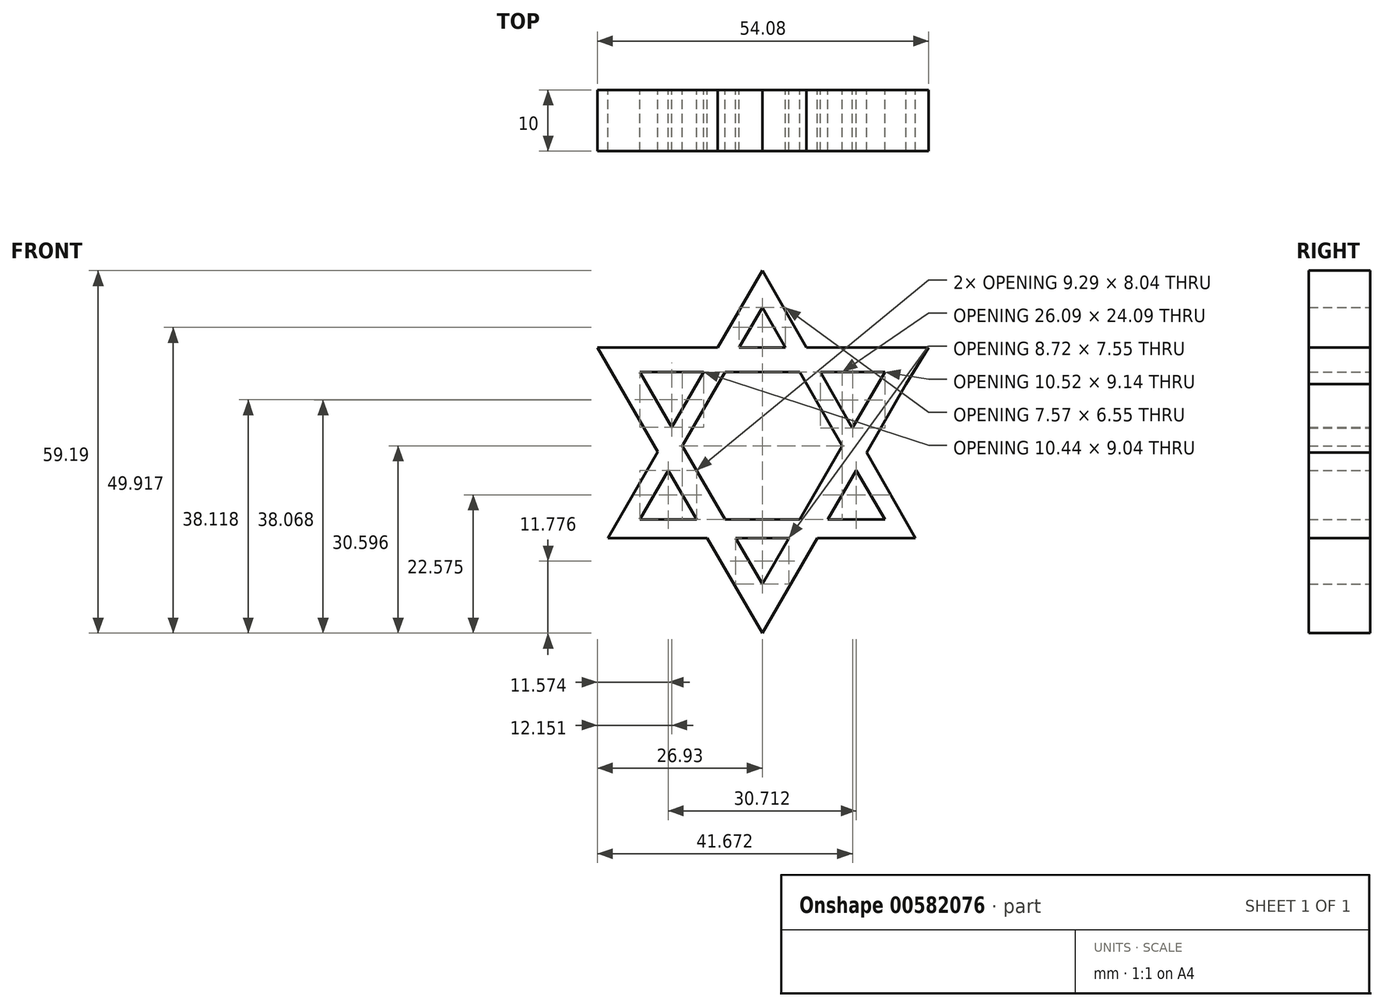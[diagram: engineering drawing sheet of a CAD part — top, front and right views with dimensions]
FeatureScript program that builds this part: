
annotation { "Feature Type Name" : "Feature", "Feature Type Description" : "" }
export const myFeature = defineFeature(function(context is Context, id is Id, definition is map)
    precondition{}
    {
        {
            var Q0;
            Q0=qCreatedBy(makeId("Front.planeOp"),FACE);
            var sketch = newSketch(context, id + "F0", { "sketchPlane" : qUnion([Q0])});
            skLineSegment(sketch, "E0", {"start": v(0, -49.6) * mm, "end": v(0, 49.74) * mm, "construction": true});
            skLineSegment(sketch, "E1", {"start": v(-9.56, 0) * mm, "end": v(56.5, 0) * mm, "construction": true});
            skLineSegment(sketch, "E2", {"start": v(0, -34.64) * mm, "end": v(-20, 0) * mm});
            skLineSegment(sketch, "E3", {"start": v(-20, 0) * mm, "end": v(20, 0) * mm});
            skLineSegment(sketch, "E4", {"start": v(20, 0) * mm, "end": v(0, -34.64) * mm});
            skLineSegment(sketch, "E5", {"start": v(-20, -24.09) * mm, "end": v(0, 10.55) * mm});
            skLineSegment(sketch, "E6", {"start": v(0, 10.55) * mm, "end": v(20, -24.09) * mm});
            skLineSegment(sketch, "E7", {"start": v(-20, -24.09) * mm, "end": v(20, -24.09) * mm});
            skLineSegment(sketch, "E8", {"start": v(25, -27.09) * mm, "end": v(-25.2, -27.09) * mm});
            skLineSegment(sketch, "E9", {"start": v(-25.2, -27.09) * mm, "end": v(0, 16.55) * mm});
            skLineSegment(sketch, "E10", {"start": v(0, 16.55) * mm, "end": v(25, -27.09) * mm});
            skLineSegment(sketch, "E11.0", {"start": v(0, -42.64) * mm, "end": v(-23.46, -2) * mm});
            skLineSegment(sketch, "E11.1", {"start": v(23.46, -2) * mm, "end": v(0, -42.64) * mm});
            skPoint(sketch, "E12.orphan", {"position": v(-51.85, 0) * mm});
            skLineSegment(sketch, "E13.0", {"start": v(-20, 4) * mm, "end": v(20, 4) * mm});
            skLineSegment(sketch, "E14", {"start": v(-23.46, -2) * mm, "end": v(-26.93, 4) * mm});
            skLineSegment(sketch, "E15", {"start": v(-26.93, 4) * mm, "end": v(-20, 4) * mm});
            skLineSegment(sketch, "E16", {"start": v(20, 4) * mm, "end": v(27.15, 4) * mm});
            skPoint(sketch, "E16.endSnap0", {"position": v(0, 4) * mm});
            skLineSegment(sketch, "E17", {"start": v(27.15, 4) * mm, "end": v(23.46, -2) * mm});
            skSolve(sketch);
        }
        {
            var Q0;
            {var subQ0=sQuery(id+"F0.wireOp",EDGE,"E7");var subQ1=sQuery(id+"F0.wireOp",EDGE,"E2");var subQ2=makeQuery(id+"F0.imprint","INTERSECT",VERTEX,{"derivedFrom":[subQ1,subQ0]});Q0=makeQuery(id+"F0.imprint","IMPRINT",FACE,{"disambiguationData":[TD([[makeQuery(id+"F0.imprint","IMPRINT",EDGE,{"disambiguationData":[TD([[subQ2,-1.0]])],"derivedFrom":subQ1}),1.0]])]});}
            var Q1;
            {var subQ3=sQuery(id+"F0.wireOp",EDGE,"E2");var subQ5=sQuery(id+"F0.wireOp",EDGE,"E4");var subQ6=makeQuery(id+"F0.imprint","INTERSECT",VERTEX,{"derivedFrom":[subQ3,subQ5]});Q1=makeQuery(id+"F0.imprint","IMPRINT",FACE,{"disambiguationData":[TD([[makeQuery(id+"F0.imprint","IMPRINT",EDGE,{"disambiguationData":[TD([[subQ6,-1.0]])],"derivedFrom":subQ3}),1.0]])]});}
            var Q2;
            {var subQ0=sQuery(id+"F0.wireOp",EDGE,"E6");var subQ1=sQuery(id+"F0.wireOp",EDGE,"E4");var subQ2=makeQuery(id+"F0.imprint","INTERSECT",VERTEX,{"derivedFrom":[subQ1,subQ0]});Q2=makeQuery(id+"F0.imprint","IMPRINT",FACE,{"disambiguationData":[TD([[makeQuery(id+"F0.imprint","IMPRINT",EDGE,{"disambiguationData":[TD([[subQ2,-1.0]])],"derivedFrom":subQ1}),1.0]])]});}
            var Q3;
            {var subQ11=sQuery(id+"F0.wireOp",EDGE,"E16");Q3=makeQuery(id+"F0.imprint","IMPRINT",FACE,{"disambiguationData":[TD([[makeQuery(id+"F0.imprint","IMPRINT",EDGE,{"derivedFrom":subQ11}),-1.0]])]});}
            var Q4;
            {var subQ0=sQuery(id+"F0.wireOp",EDGE,"E5");var subQ1=sQuery(id+"F0.wireOp",EDGE,"E3");var subQ2=makeQuery(id+"F0.imprint","INTERSECT",VERTEX,{"derivedFrom":[subQ1,subQ0]});Q4=makeQuery(id+"F0.imprint","IMPRINT",FACE,{"disambiguationData":[TD([[makeQuery(id+"F0.imprint","IMPRINT",EDGE,{"disambiguationData":[TD([[subQ2,-1.0]])],"derivedFrom":subQ1}),1.0]])]});}
            var Q5;
            {var subQ7=sQuery(id+"F0.wireOp",EDGE,"E14");Q5=makeQuery(id+"F0.imprint","IMPRINT",FACE,{"disambiguationData":[TD([[makeQuery(id+"F0.imprint","IMPRINT",EDGE,{"derivedFrom":subQ7}),-1.0]])]});}
            var Q6;
            {var subQ0=sQuery(id+"F0.wireOp",EDGE,"E5");var subQ1=sQuery(id+"F0.wireOp",EDGE,"E2");var subQ2=makeQuery(id+"F0.imprint","INTERSECT",VERTEX,{"derivedFrom":[subQ1,subQ0]});Q6=makeQuery(id+"F0.imprint","IMPRINT",FACE,{"disambiguationData":[TD([[makeQuery(id+"F0.imprint","IMPRINT",EDGE,{"disambiguationData":[TD([[subQ2,-1.0]])],"derivedFrom":subQ1}),1.0]])]});}
            var Q7;
            {var subQ0=sQuery(id+"F0.wireOp",EDGE,"E8");var subQ1=sQuery(id+"F0.wireOp",EDGE,"E2");var subQ2=makeQuery(id+"F0.imprint","INTERSECT",VERTEX,{"derivedFrom":[subQ1,subQ0]});Q7=makeQuery(id+"F0.imprint","IMPRINT",FACE,{"disambiguationData":[TD([[makeQuery(id+"F0.imprint","IMPRINT",EDGE,{"disambiguationData":[TD([[subQ2,-1.0]])],"derivedFrom":subQ1}),1.0]])]});}
            var Q8;
            {var subQ0=sQuery(id+"F0.wireOp",EDGE,"E7");var subQ1=sQuery(id+"F0.wireOp",EDGE,"E4");var subQ2=makeQuery(id+"F0.imprint","INTERSECT",VERTEX,{"derivedFrom":[subQ1,subQ0]});Q8=makeQuery(id+"F0.imprint","IMPRINT",FACE,{"disambiguationData":[TD([[makeQuery(id+"F0.imprint","IMPRINT",EDGE,{"disambiguationData":[TD([[subQ2,-1.0]])],"derivedFrom":subQ1}),1.0]])]});}
            var Q9;
            {var subQ0=sQuery(id+"F0.wireOp",EDGE,"E10");var subQ1=sQuery(id+"F0.wireOp",EDGE,"E4");var subQ2=makeQuery(id+"F0.imprint","INTERSECT",VERTEX,{"derivedFrom":[subQ1,subQ0]});Q9=makeQuery(id+"F0.imprint","IMPRINT",FACE,{"disambiguationData":[TD([[makeQuery(id+"F0.imprint","IMPRINT",EDGE,{"disambiguationData":[TD([[subQ2,-1.0]])],"derivedFrom":subQ1}),1.0]])]});}
            var Q10;
            {var subQ0=sQuery(id+"F0.wireOp",EDGE,"E6");var subQ1=sQuery(id+"F0.wireOp",EDGE,"E3");var subQ2=makeQuery(id+"F0.imprint","INTERSECT",VERTEX,{"derivedFrom":[subQ1,subQ0]});Q10=makeQuery(id+"F0.imprint","IMPRINT",FACE,{"disambiguationData":[TD([[makeQuery(id+"F0.imprint","IMPRINT",EDGE,{"disambiguationData":[TD([[subQ2,-1.0]])],"derivedFrom":subQ1}),1.0]])]});}
            var Q11;
            {var subQ0=sQuery(id+"F0.wireOp",EDGE,"E9");var subQ1=sQuery(id+"F0.wireOp",EDGE,"E3");var subQ2=makeQuery(id+"F0.imprint","INTERSECT",VERTEX,{"derivedFrom":[subQ1,subQ0]});Q11=makeQuery(id+"F0.imprint","IMPRINT",FACE,{"disambiguationData":[TD([[makeQuery(id+"F0.imprint","IMPRINT",EDGE,{"disambiguationData":[TD([[subQ2,-1.0]])],"derivedFrom":subQ1}),1.0]])]});}
            var Q12;
            {var subQ0=sQuery(id+"F0.wireOp",EDGE,"E5");var subQ1=sQuery(id+"F0.wireOp",EDGE,"E2");var subQ2=makeQuery(id+"F0.imprint","INTERSECT",VERTEX,{"derivedFrom":[subQ1,subQ0]});Q12=makeQuery(id+"F0.imprint","IMPRINT",FACE,{"disambiguationData":[TD([[makeQuery(id+"F0.imprint","IMPRINT",EDGE,{"disambiguationData":[TD([[subQ2,-1.0]])],"derivedFrom":subQ1}),-1.0]])]});}
            var Q13;
            {var subQ6=sQuery(id+"F0.wireOp",EDGE,"E7");var subQ8=sQuery(id+"F0.wireOp",EDGE,"E5");var subQ9=makeQuery(id+"F0.imprint","INTERSECT",VERTEX,{"derivedFrom":[subQ8,subQ6]});Q13=makeQuery(id+"F0.imprint","IMPRINT",FACE,{"disambiguationData":[TD([[makeQuery(id+"F0.imprint","IMPRINT",EDGE,{"disambiguationData":[TD([[subQ9,-1.0]])],"derivedFrom":subQ8}),1.0]])]});}
            var Q14;
            {var subQ0=sQuery(id+"F0.wireOp",EDGE,"E8");var subQ1=sQuery(id+"F0.wireOp",EDGE,"E2");var subQ2=makeQuery(id+"F0.imprint","INTERSECT",VERTEX,{"derivedFrom":[subQ1,subQ0]});Q14=makeQuery(id+"F0.imprint","IMPRINT",FACE,{"disambiguationData":[TD([[makeQuery(id+"F0.imprint","IMPRINT",EDGE,{"disambiguationData":[TD([[subQ2,-1.0]])],"derivedFrom":subQ1}),-1.0]])]});}
            var Q15;
            {var subQ6=sQuery(id+"F0.wireOp",EDGE,"E7");var subQ7=sQuery(id+"F0.wireOp",EDGE,"E6");var subQ8=makeQuery(id+"F0.imprint","INTERSECT",VERTEX,{"derivedFrom":[subQ7,subQ6]});Q15=makeQuery(id+"F0.imprint","IMPRINT",FACE,{"disambiguationData":[TD([[makeQuery(id+"F0.imprint","IMPRINT",EDGE,{"disambiguationData":[TD([[subQ8,1.0]])],"derivedFrom":subQ7}),1.0]])]});}
            var Q16;
            {var subQ0=sQuery(id+"F0.wireOp",EDGE,"E6");var subQ1=sQuery(id+"F0.wireOp",EDGE,"E3");var subQ2=makeQuery(id+"F0.imprint","INTERSECT",VERTEX,{"derivedFrom":[subQ1,subQ0]});Q16=makeQuery(id+"F0.imprint","IMPRINT",FACE,{"disambiguationData":[TD([[makeQuery(id+"F0.imprint","IMPRINT",EDGE,{"disambiguationData":[TD([[subQ2,-1.0]])],"derivedFrom":subQ1}),-1.0]])]});}
            var Q17;
            {var subQ5=sQuery(id+"F0.wireOp",EDGE,"E6");var subQ6=sQuery(id+"F0.wireOp",EDGE,"E5");var subQ7=makeQuery(id+"F0.imprint","INTERSECT",VERTEX,{"derivedFrom":[subQ6,subQ5]});Q17=makeQuery(id+"F0.imprint","IMPRINT",FACE,{"disambiguationData":[TD([[makeQuery(id+"F0.imprint","IMPRINT",EDGE,{"disambiguationData":[TD([[subQ7,1.0]])],"derivedFrom":subQ6}),1.0]])]});}
            extrude(context, id + "F1", {"entities" : qUnion([Q0, Q1, Q2, Q3, Q4, Q5, Q6, Q7, Q8, Q9, Q10, Q11, Q12, Q13, Q14, Q15, Q16, Q17]), "depth" : 10 * mm, "offsetDistance" : 25 * mm});
        }
    });
